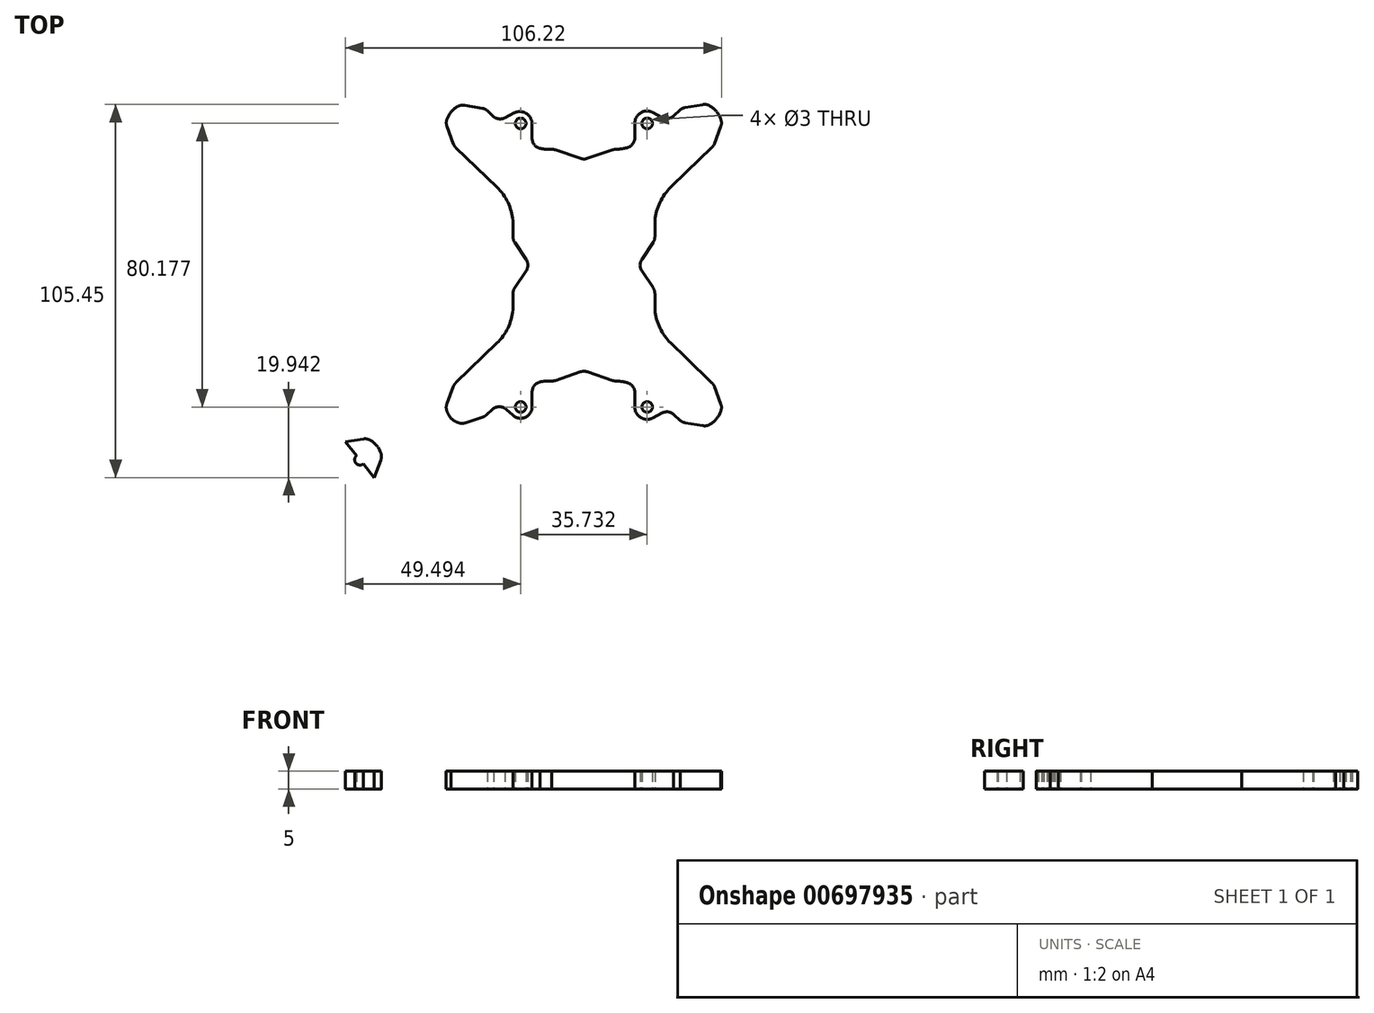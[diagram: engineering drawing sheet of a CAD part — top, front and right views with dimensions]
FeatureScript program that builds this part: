
annotation { "Feature Type Name" : "Feature", "Feature Type Description" : "" }
export const myFeature = defineFeature(function(context is Context, id is Id, definition is map)
    precondition{}
    {
        {
            var Q0;
            Q0=qCreatedBy(makeId("Top.planeOp"),FACE);
            var sketch = newSketch(context, id + "F0", { "sketchPlane" : qUnion([Q0])});
            skArc(sketch, "E0.MirrorCS", {"start": v(27.18, 43.9) * mm, "mid": v(27.85, 44.3) * mm, "end": v(28.6, 44.54) * mm});
            skLineSegment(sketch, "E1.MirrorCS", {"start": v(27.18, 43.9) * mm, "end": v(25.36, 42.14) * mm});
            skArc(sketch, "E2.MirrorCS", {"start": v(38.59, 41.43) * mm, "mid": v(38.86, 40.33) * mm, "end": v(38.7, 39.21) * mm});
            skArc(sketch, "E3.MirrorCS", {"start": v(33.61, 45.38) * mm, "mid": v(34.66, 45.37) * mm, "end": v(35.65, 45) * mm});
            skLineSegment(sketch, "E4.MirrorCS", {"start": v(36.87, 34.33) * mm, "end": v(38.7, 39.21) * mm});
            skLineSegment(sketch, "E5.MirrorCS", {"start": v(28.6, 44.54) * mm, "end": v(33.61, 45.38) * mm});
            skCircle(sketch, "E6.MirrorC", {"center": v(17.87, 40.09) * mm, "radius": 1.5 * mm});
            skArc(sketch, "E7.MirrorCS", {"start": v(35.65, 45) * mm, "mid": v(37.43, 43.47) * mm, "end": v(38.59, 41.43) * mm});
            skArc(sketch, "E8.MirrorCS", {"start": v(14.39, 36.08) * mm, "mid": v(13.74, 34.22) * mm, "end": v(12.09, 33.16) * mm});
            skLineSegment(sketch, "E9.MirrorCS", {"start": v(36.14, 33.23) * mm, "end": v(35.6, 32.7) * mm});
            skArc(sketch, "E10.MirrorCS", {"start": v(36.87, 34.33) * mm, "mid": v(36.57, 33.74) * mm, "end": v(36.14, 33.23) * mm});
            skArc(sketch, "E11.MirrorCS", {"start": v(9, 32.75) * mm, "mid": v(10.56, 32.88) * mm, "end": v(12.09, 33.16) * mm});
            skLineSegment(sketch, "E12.MirrorCS", {"start": v(14.39, 40.46) * mm, "end": v(14.39, 36.08) * mm});
            skLineSegment(sketch, "E13.MirrorCS", {"start": v(19.53, 43.17) * mm, "end": v(22.03, 41.82) * mm});
            skLineSegment(sketch, "E14.MirrorCS", {"start": v(29.02, 26.35) * mm, "end": v(24.57, 22.03) * mm});
            skArc(sketch, "E15.MirrorCS", {"start": v(25.36, 42.14) * mm, "mid": v(23.75, 41.47) * mm, "end": v(22.03, 41.82) * mm});
            skPoint(sketch, "E16.MirrorP", {"position": v(18, 22.67) * mm});
            skPoint(sketch, "E17.MirrorP", {"position": v(18.1, 36.17) * mm});
            skPoint(sketch, "E18.MirrorP", {"position": v(27.93, 44.26) * mm});
            skPoint(sketch, "E19.MirrorP", {"position": v(20, 17.65) * mm});
            skLineSegment(sketch, "E20.MirrorCS", {"start": v(35.6, 32.7) * mm, "end": v(29.02, 26.35) * mm});
            skPoint(sketch, "E21.MirrorP", {"position": v(20, 20) * mm});
            skPoint(sketch, "E22.MirrorP", {"position": v(34.26, 31.4) * mm});
            skPoint(sketch, "E23.MirrorP", {"position": v(18.25, 22.92) * mm});
            skArc(sketch, "E24.MirrorCS", {"start": v(14.39, 40.46) * mm, "mid": v(16.23, 43.18) * mm, "end": v(19.53, 43.17) * mm});
            skPoint(sketch, "E25.MirrorP", {"position": v(34.66, 45.39) * mm});
            skPoint(sketch, "E26.MirrorP", {"position": v(14.39, 33.92) * mm});
            skPoint(sketch, "E27.MirrorP", {"position": v(21.82, 21.5) * mm});
            skPoint(sketch, "E28.MirrorP", {"position": v(39.03, 40.08) * mm});
            skPoint(sketch, "E29.MirrorP", {"position": v(36.63, 33.7) * mm});
            skPoint(sketch, "E30.MirrorP", {"position": v(32.97, 48.4) * mm});
            skPoint(sketch, "E31.MirrorP", {"position": v(23.8, 40.86) * mm});
            skPoint(sketch, "E32.MirrorP", {"position": v(30.36, 27.65) * mm});
            skArc(sketch, "E33.MirrorCS", {"start": v(-27.3, 43.71) * mm, "mid": v(-27.97, 44.13) * mm, "end": v(-28.72, 44.35) * mm});
            skLineSegment(sketch, "E34.MirrorCS", {"start": v(-27.3, 43.71) * mm, "end": v(-25.49, 41.96) * mm});
            skCircle(sketch, "E35.MirrorC", {"center": v(-17.87, 40.09) * mm, "radius": 1.5 * mm});
            skArc(sketch, "E36.MirrorCS", {"start": v(-36.86, 34.3) * mm, "mid": v(-36.56, 33.7) * mm, "end": v(-36.13, 33.2) * mm});
            skLineSegment(sketch, "E37.MirrorCS", {"start": v(-36.13, 33.2) * mm, "end": v(-35.6, 32.67) * mm});
            skArc(sketch, "E38.MirrorCS", {"start": v(-33.74, 45.2) * mm, "mid": v(-34.79, 45.19) * mm, "end": v(-35.77, 44.82) * mm});
            skLineSegment(sketch, "E39.MirrorCS", {"start": v(-36.86, 34.3) * mm, "end": v(-38.7, 39.18) * mm});
            skLineSegment(sketch, "E40.MirrorCS", {"start": v(-28.72, 44.35) * mm, "end": v(-33.74, 45.2) * mm});
            skArc(sketch, "E41.MirrorCS", {"start": v(-38.71, 41.24) * mm, "mid": v(-38.89, 40.2) * mm, "end": v(-38.7, 39.18) * mm});
            skArc(sketch, "E42.MirrorCS", {"start": v(-35.77, 44.82) * mm, "mid": v(-37.55, 43.29) * mm, "end": v(-38.71, 41.24) * mm});
            skLineSegment(sketch, "E43.MirrorCS", {"start": v(-19.8, 42.98) * mm, "end": v(-22.3, 41.63) * mm});
            skArc(sketch, "E44.MirrorCS", {"start": v(-25.49, 41.96) * mm, "mid": v(-23.94, 41.33) * mm, "end": v(-22.3, 41.63) * mm});
            skLineSegment(sketch, "E45.MirrorCS", {"start": v(-29.01, 26.32) * mm, "end": v(-24.57, 22.03) * mm});
            skArc(sketch, "E46.MirrorCS", {"start": v(-14.65, 35.9) * mm, "mid": v(-14, 34.04) * mm, "end": v(-12.35, 32.98) * mm});
            skArc(sketch, "E47.MirrorCS", {"start": v(-14.65, 40.27) * mm, "mid": v(-16.5, 43) * mm, "end": v(-19.8, 42.98) * mm});
            skLineSegment(sketch, "E48.MirrorCS", {"start": v(-14.65, 40.27) * mm, "end": v(-14.65, 35.9) * mm});
            skArc(sketch, "E49.MirrorCS", {"start": v(-20.05, 12.63) * mm, "mid": v(-21.47, 17.74) * mm, "end": v(-24.57, 22.03) * mm});
            skPoint(sketch, "E50.MirrorP", {"position": v(-18.1, 36.17) * mm});
            skLineSegment(sketch, "E51.MirrorCS", {"start": v(-35.6, 32.67) * mm, "end": v(-29.01, 26.32) * mm});
            skArc(sketch, "E52.MirrorCS", {"start": v(-9.14, 32.75) * mm, "mid": v(-10.75, 32.78) * mm, "end": v(-12.35, 32.98) * mm});
            skPoint(sketch, "E53.MirrorP", {"position": v(-20, 20) * mm});
            skPoint(sketch, "E54.MirrorP", {"position": v(-27.93, 44.26) * mm});
            skPoint(sketch, "E55.MirrorP", {"position": v(-20, 17.65) * mm});
            skPoint(sketch, "E56.MirrorP", {"position": v(-32.97, 48.4) * mm});
            skPoint(sketch, "E57.MirrorP", {"position": v(-30.36, 27.65) * mm});
            skPoint(sketch, "E58.MirrorP", {"position": v(-21.82, 21.5) * mm});
            skPoint(sketch, "E59.MirrorP", {"position": v(-23.8, 40.86) * mm});
            skPoint(sketch, "E60.MirrorP", {"position": v(-39.03, 40.08) * mm});
            skPoint(sketch, "E61.MirrorP", {"position": v(-34.26, 31.4) * mm});
            skPoint(sketch, "E62.MirrorP", {"position": v(-18, 22.67) * mm});
            skPoint(sketch, "E63.MirrorP", {"position": v(-14.39, 33.92) * mm});
            skPoint(sketch, "E64.MirrorP", {"position": v(-18.25, 22.92) * mm});
            skPoint(sketch, "E65.MirrorP", {"position": v(-36.63, 33.7) * mm});
            skPoint(sketch, "E66.MirrorP", {"position": v(-34.66, 45.39) * mm});
            skLineSegment(sketch, "E67.MirrorCS", {"start": v(-8.13, 32.6) * mm, "end": v(-0.97, 30.16) * mm});
            skLineSegment(sketch, "E68.MirrorCS", {"start": v(0.97, 30.16) * mm, "end": v(8.13, 32.6) * mm});
            skArc(sketch, "E69.MirrorCS", {"start": v(-9.14, 32.75) * mm, "mid": v(-8.63, 32.72) * mm, "end": v(-8.13, 32.6) * mm});
            skArc(sketch, "E70.MirrorCS", {"start": v(8.13, 32.6) * mm, "mid": v(8.56, 32.7) * mm, "end": v(9, 32.75) * mm});
            skArc(sketch, "E71.MirrorCS", {"start": v(0.97, 30.16) * mm, "mid": v(0, 30) * mm, "end": v(-0.97, 30.16) * mm});
            skPoint(sketch, "E72.orphan", {"position": v(8.57, 32.75) * mm});
            skPoint(sketch, "E73.orphan", {"position": v(-9.7, 32.74) * mm});
            skLineSegment(sketch, "E74", {"start": v(0, 30.16) * mm, "end": v(0, 30) * mm});
            skPoint(sketch, "E74.startSnap0", {"position": v(0, 30) * mm});
            skArc(sketch, "E75.MirrorCS", {"start": v(20.05, 12.63) * mm, "mid": v(21.47, 17.74) * mm, "end": v(24.57, 22.03) * mm});
            skLineSegment(sketch, "E76", {"start": v(-19.55, 6.41) * mm, "end": v(-16.36, 1.67) * mm});
            skLineSegment(sketch, "E77.MirrorCS", {"start": v(19.55, 6.41) * mm, "end": v(16.36, 1.67) * mm});
            skLineSegment(sketch, "E78.trimOffspring", {"start": v(-20.05, 8.08) * mm, "end": v(-20.05, 12.63) * mm});
            skLineSegment(sketch, "E79.trimOffspring", {"start": v(20.05, 8.08) * mm, "end": v(20.05, 12.63) * mm});
            skPoint(sketch, "E80.visualSharp", {"position": v(-20.05, 7.17) * mm});
            skArc(sketch, "E80.filletArc", {"start": v(-20.05, 8.08) * mm, "mid": v(-19.92, 7.21) * mm, "end": v(-19.55, 6.41) * mm});
            skPoint(sketch, "E81.visualSharp", {"position": v(-15.24, 0) * mm});
            skArc(sketch, "E81.filletArc", {"start": v(-16.36, -1.67) * mm, "mid": v(-15.85, 0) * mm, "end": v(-16.36, 1.67) * mm});
            skPoint(sketch, "E82.visualSharp", {"position": v(20.05, 7.17) * mm});
            skArc(sketch, "E82.filletArc", {"start": v(19.55, 6.41) * mm, "mid": v(19.92, 7.21) * mm, "end": v(20.05, 8.08) * mm});
            skPoint(sketch, "E83.visualSharp", {"position": v(15.24, 0) * mm});
            skArc(sketch, "E83.filletArc", {"start": v(16.36, 1.67) * mm, "mid": v(15.85, 0) * mm, "end": v(16.36, -1.67) * mm});
            skLineSegment(sketch, "E84.bottom", {"start": v(-19.98, 42.28) * mm, "end": v(19.98, 42.28) * mm, "construction": true});
            skLineSegment(sketch, "E84.left", {"start": v(-19.98, 42.28) * mm, "end": v(-19.98, -42.28) * mm, "construction": true});
            skLineSegment(sketch, "E84.right", {"start": v(19.98, 42.28) * mm, "end": v(19.98, -42.28) * mm, "construction": true});
            skPoint(sketch, "E84.middle", {"position": v(0, 0) * mm});
            skLineSegment(sketch, "E85.MirrorCS", {"start": v(0, -30.16) * mm, "end": v(0, -30) * mm});
            skLineSegment(sketch, "E86.MirrorCS", {"start": v(0.97, -30.16) * mm, "end": v(8.13, -32.6) * mm});
            skArc(sketch, "E87.MirrorCS", {"start": v(-36.86, -34.3) * mm, "mid": v(-36.56, -33.7) * mm, "end": v(-36.13, -33.2) * mm});
            skLineSegment(sketch, "E88.MirrorCS", {"start": v(36.14, -33.23) * mm, "end": v(35.6, -32.7) * mm});
            skArc(sketch, "E89.MirrorCS", {"start": v(-9.14, -32.75) * mm, "mid": v(-8.63, -32.72) * mm, "end": v(-8.13, -32.6) * mm});
            skArc(sketch, "E90.MirrorCS", {"start": v(8.13, -32.6) * mm, "mid": v(8.56, -32.7) * mm, "end": v(9, -32.75) * mm});
            skArc(sketch, "E91.MirrorCS", {"start": v(-9.14, -32.75) * mm, "mid": v(-10.75, -32.78) * mm, "end": v(-12.35, -32.98) * mm});
            skArc(sketch, "E92.MirrorCS", {"start": v(0.97, -30.16) * mm, "mid": v(0, -30) * mm, "end": v(-0.97, -30.16) * mm});
            skLineSegment(sketch, "E93.MirrorCS", {"start": v(-36.13, -33.2) * mm, "end": v(-35.6, -32.67) * mm});
            skArc(sketch, "E94.MirrorCS", {"start": v(36.87, -34.33) * mm, "mid": v(36.57, -33.74) * mm, "end": v(36.14, -33.23) * mm});
            skArc(sketch, "E95.MirrorCS", {"start": v(9, -32.75) * mm, "mid": v(10.56, -32.88) * mm, "end": v(12.09, -33.16) * mm});
            skArc(sketch, "E96.MirrorCS", {"start": v(-20.05, -8.08) * mm, "mid": v(-19.92, -7.21) * mm, "end": v(-19.55, -6.41) * mm});
            skLineSegment(sketch, "E97.MirrorCS", {"start": v(36.87, -34.33) * mm, "end": v(38.7, -39.21) * mm});
            skLineSegment(sketch, "E98.MirrorCS", {"start": v(27.18, -43.9) * mm, "end": v(25.36, -42.14) * mm});
            skArc(sketch, "E99.MirrorCS", {"start": v(25.36, -42.14) * mm, "mid": v(23.75, -41.47) * mm, "end": v(22.03, -41.82) * mm});
            skLineSegment(sketch, "E100.MirrorCS", {"start": v(19.53, -43.17) * mm, "end": v(22.03, -41.82) * mm});
            skArc(sketch, "E101.MirrorCS", {"start": v(38.59, -41.43) * mm, "mid": v(38.86, -40.33) * mm, "end": v(38.7, -39.21) * mm});
            skArc(sketch, "E102.MirrorCS", {"start": v(27.18, -43.9) * mm, "mid": v(27.85, -44.3) * mm, "end": v(28.6, -44.54) * mm});
            skLineSegment(sketch, "E103.MirrorCS", {"start": v(-20.05, -8.08) * mm, "end": v(-20.05, -12.63) * mm});
            skLineSegment(sketch, "E104.MirrorCS", {"start": v(20.05, -8.08) * mm, "end": v(20.05, -12.63) * mm});
            skLineSegment(sketch, "E105.MirrorCS", {"start": v(-35.6, -32.67) * mm, "end": v(-29.01, -26.32) * mm});
            skArc(sketch, "E106.MirrorCS", {"start": v(19.55, -6.41) * mm, "mid": v(19.92, -7.21) * mm, "end": v(20.05, -8.08) * mm});
            skCircle(sketch, "E107.MirrorC", {"center": v(17.87, -40.09) * mm, "radius": 1.5 * mm});
            skLineSegment(sketch, "E108.MirrorCS", {"start": v(19.55, -6.41) * mm, "end": v(16.36, -1.67) * mm});
            skArc(sketch, "E109.MirrorCS", {"start": v(-14.65, -35.9) * mm, "mid": v(-14, -34.04) * mm, "end": v(-12.35, -32.98) * mm});
            skArc(sketch, "E110.MirrorCS", {"start": v(20.05, -12.63) * mm, "mid": v(21.47, -17.74) * mm, "end": v(24.57, -22.03) * mm});
            skArc(sketch, "E111.MirrorCS", {"start": v(35.65, -45) * mm, "mid": v(37.43, -43.47) * mm, "end": v(38.59, -41.43) * mm});
            skArc(sketch, "E112.MirrorCS", {"start": v(-37.55, -43.29) * mm, "mid": v(-38.22, -42.32) * mm, "end": v(-38.71, -41.24) * mm});
            skLineSegment(sketch, "E113.MirrorCS", {"start": v(14.39, -40.46) * mm, "end": v(14.39, -36.08) * mm});
            skLineSegment(sketch, "E114.MirrorCS", {"start": v(29.02, -26.35) * mm, "end": v(24.57, -22.03) * mm});
            skLineSegment(sketch, "E115.MirrorCS", {"start": v(-8.13, -32.6) * mm, "end": v(-0.97, -30.16) * mm});
            skArc(sketch, "E116.MirrorCS", {"start": v(14.39, -40.46) * mm, "mid": v(16.23, -43.18) * mm, "end": v(19.53, -43.17) * mm});
            skArc(sketch, "E117.MirrorCS", {"start": v(-38.71, -41.24) * mm, "mid": v(-38.89, -40.2) * mm, "end": v(-38.7, -39.18) * mm});
            skLineSegment(sketch, "E118.MirrorCS", {"start": v(35.6, -32.7) * mm, "end": v(29.02, -26.35) * mm});
            skArc(sketch, "E119.MirrorCS", {"start": v(-20.05, -12.63) * mm, "mid": v(-21.47, -17.74) * mm, "end": v(-24.57, -22.03) * mm});
            skLineSegment(sketch, "E120.MirrorCS", {"start": v(-29.01, -26.32) * mm, "end": v(-24.57, -22.03) * mm});
            skCircle(sketch, "E121.MirrorC", {"center": v(-17.87, -40.09) * mm, "radius": 1.5 * mm});
            skArc(sketch, "E122.MirrorCS", {"start": v(14.39, -36.08) * mm, "mid": v(13.74, -34.22) * mm, "end": v(12.09, -33.16) * mm});
            skArc(sketch, "E123.MirrorCS", {"start": v(33.61, -45.38) * mm, "mid": v(34.66, -45.37) * mm, "end": v(35.65, -45) * mm});
            skLineSegment(sketch, "E124.MirrorCS", {"start": v(-14.65, -40.27) * mm, "end": v(-14.65, -35.9) * mm});
            skLineSegment(sketch, "E125.MirrorCS", {"start": v(28.6, -44.54) * mm, "end": v(33.61, -45.38) * mm});
            skArc(sketch, "E126.MirrorCS", {"start": v(-14.65, -40.27) * mm, "mid": v(-14.69, -40.56) * mm, "end": v(-14.76, -40.84) * mm});
            skLineSegment(sketch, "E127.MirrorCS", {"start": v(-36.86, -34.3) * mm, "end": v(-38.7, -39.18) * mm});
            skLineSegment(sketch, "E128.MirrorCS", {"start": v(-19.55, -6.41) * mm, "end": v(-16.36, -1.67) * mm});
            skPoint(sketch, "E129.MirrorP", {"position": v(23.8, -40.86) * mm});
            skPoint(sketch, "E130.MirrorP", {"position": v(20, -20) * mm});
            skPoint(sketch, "E131.MirrorP", {"position": v(-18.1, -36.17) * mm});
            skPoint(sketch, "E132.MirrorP", {"position": v(18.1, -36.17) * mm});
            skPoint(sketch, "E133.MirrorP", {"position": v(8.57, -32.75) * mm});
            skPoint(sketch, "E134.MirrorP", {"position": v(-27.93, -44.26) * mm});
            skPoint(sketch, "E135.MirrorP", {"position": v(-20, -17.65) * mm});
            skPoint(sketch, "E136.MirrorP", {"position": v(20, -17.65) * mm});
            skPoint(sketch, "E137.MirrorP", {"position": v(27.93, -44.26) * mm});
            skPoint(sketch, "E138.MirrorP", {"position": v(-20.05, -7.17) * mm});
            skPoint(sketch, "E139.MirrorP", {"position": v(18.25, -22.92) * mm});
            skPoint(sketch, "E140.MirrorP", {"position": v(39.03, -40.08) * mm});
            skPoint(sketch, "E141.MirrorP", {"position": v(-34.66, -45.39) * mm});
            skPoint(sketch, "E142.MirrorP", {"position": v(-9.7, -32.74) * mm});
            skPoint(sketch, "E143.MirrorP", {"position": v(14.39, -33.92) * mm});
            skPoint(sketch, "E144.MirrorP", {"position": v(-18.25, -22.92) * mm});
            skPoint(sketch, "E145.MirrorP", {"position": v(0, -30) * mm});
            skPoint(sketch, "E146.MirrorP", {"position": v(-30.36, -27.65) * mm});
            skLineSegment(sketch, "E147.MirrorCS", {"start": v(-19.98, -42.28) * mm, "end": v(19.98, -42.28) * mm, "construction": true});
            skPoint(sketch, "E148.MirrorP", {"position": v(-18, -22.67) * mm});
            skPoint(sketch, "E149.MirrorP", {"position": v(-21.82, -21.5) * mm});
            skPoint(sketch, "E150.MirrorP", {"position": v(21.82, -21.5) * mm});
            skPoint(sketch, "E151.MirrorP", {"position": v(-34.26, -31.4) * mm});
            skPoint(sketch, "E152.MirrorP", {"position": v(36.63, -33.7) * mm});
            skPoint(sketch, "E153.MirrorP", {"position": v(34.66, -45.39) * mm});
            skPoint(sketch, "E154.MirrorP", {"position": v(-36.63, -33.7) * mm});
            skPoint(sketch, "E155.MirrorP", {"position": v(-32.97, -48.4) * mm});
            skPoint(sketch, "E156.MirrorP", {"position": v(18, -22.67) * mm});
            skPoint(sketch, "E157.MirrorP", {"position": v(32.97, -48.4) * mm});
            skPoint(sketch, "E158.MirrorP", {"position": v(30.36, -27.65) * mm});
            skPoint(sketch, "E159.MirrorP", {"position": v(20.05, -7.17) * mm});
            skPoint(sketch, "E160.MirrorP", {"position": v(-14.39, -33.92) * mm});
            skPoint(sketch, "E161.MirrorP", {"position": v(-39.03, -40.08) * mm});
            skPoint(sketch, "E162.MirrorP", {"position": v(34.26, -31.4) * mm});
            skPoint(sketch, "E163.MirrorP", {"position": v(-20, -20) * mm});
            skArc(sketch, "E164.MirrorCS", {"start": v(-59.22, -60.03) * mm, "mid": v(-59.52, -60.62) * mm, "end": v(-59.95, -61.13) * mm});
            skLineSegment(sketch, "E165.MirrorCS", {"start": v(-59.95, -61.13) * mm, "end": v(-60.49, -61.66) * mm});
            skLineSegment(sketch, "E166.MirrorCS", {"start": v(-60.49, -61.66) * mm, "end": v(-67.07, -68) * mm});
            skArc(sketch, "E167.MirrorCS", {"start": v(-62.34, -49.13) * mm, "mid": v(-61.3, -49.14) * mm, "end": v(-60.3, -49.5) * mm});
            skLineSegment(sketch, "E168.MirrorCS", {"start": v(-67.36, -49.97) * mm, "end": v(-62.34, -49.13) * mm});
            skArc(sketch, "E169.MirrorCS", {"start": v(-60.3, -49.5) * mm, "mid": v(-58.53, -51.04) * mm, "end": v(-57.37, -53.08) * mm});
            skArc(sketch, "E170.MirrorCS", {"start": v(-57.37, -53.08) * mm, "mid": v(-57.2, -54.12) * mm, "end": v(-57.38, -55.15) * mm});
            skArc(sketch, "E171.MirrorCS", {"start": v(-68.77, -50.61) * mm, "mid": v(-68.1, -50.2) * mm, "end": v(-67.36, -49.97) * mm});
            skLineSegment(sketch, "E172.MirrorCS", {"start": v(-59.22, -60.03) * mm, "end": v(-57.38, -55.15) * mm});
            skPoint(sketch, "E173.MirrorP", {"position": v(-68.14, -50.07) * mm});
            skPoint(sketch, "E174.MirrorP", {"position": v(-61.42, -48.94) * mm});
            skPoint(sketch, "E175.MirrorP", {"position": v(-59.45, -60.63) * mm});
            skPoint(sketch, "E176.MirrorP", {"position": v(-63.11, -45.93) * mm});
            skPoint(sketch, "E177.MirrorP", {"position": v(-57.05, -54.25) * mm});
            skLineSegment(sketch, "E178", {"start": v(-59.22, -60.03) * mm, "end": v(-67.36, -49.97) * mm});
            skPoint(sketch, "E179", {"position": v(-63.3, -55) * mm});
            skCircle(sketch, "E180", {"center": v(-63.3, -55) * mm, "radius": 1.5 * mm});
            skLineSegment(sketch, "E181", {"start": v(-63.3, -55) * mm, "end": v(-69.86, -61.34) * mm});
            skLineSegment(sketch, "E182.MirrorCS", {"start": v(-69.84, -51.96) * mm, "end": v(-76.42, -58.31) * mm});
            skLineSegment(sketch, "E183", {"start": v(-37.55, -43.29) * mm, "end": v(19.17, 11.45) * mm, "construction": true});
            skLineSegment(sketch, "E184.MirrorCS", {"start": v(-28.54, -42.91) * mm, "end": v(-33.49, -44.58) * mm});
            skArc(sketch, "E185.MirrorCS", {"start": v(-35.55, -44.52) * mm, "mid": v(-34.52, -44.73) * mm, "end": v(-33.49, -44.58) * mm});
            skArc(sketch, "E186.MirrorCS", {"start": v(-37.55, -43.29) * mm, "mid": v(-36.6, -44) * mm, "end": v(-35.55, -44.52) * mm});
            skPoint(sketch, "E187.orphan", {"position": v(-39.02, -41.45) * mm});
            skPoint(sketch, "E188.MirrorCS.end.orphan", {"position": v(-35.77, -44.82) * mm});
            skPoint(sketch, "E189.MirrorCS.end.orphan", {"position": v(-33.74, -45.2) * mm});
            skPoint(sketch, "E190.MirrorCS.end.orphan", {"position": v(-28.72, -44.35) * mm});
            skPoint(sketch, "E191.MirrorCS.start.orphan", {"position": v(-27.3, -43.71) * mm});
            skArc(sketch, "E192.MirrorCS", {"start": v(-28.54, -42.91) * mm, "mid": v(-27.94, -42.63) * mm, "end": v(-27.41, -42.23) * mm});
            skLineSegment(sketch, "E193.MirrorCS", {"start": v(-27.41, -42.23) * mm, "end": v(-26.87, -41.7) * mm});
            skPoint(sketch, "E194.MirrorCS.start.orphan", {"position": v(-25.49, -41.96) * mm});
            skLineSegment(sketch, "E195", {"start": v(-26.87, -41.7) * mm, "end": v(-26.02, -40.88) * mm});
            skPoint(sketch, "E196.visualSharp", {"position": v(-19.8, -42.98) * mm});
            skArc(sketch, "E197.0", {"start": v(-14.76, -40.84) * mm, "mid": v(-16.95, -43.15) * mm, "end": v(-20.05, -42.42) * mm});
            skLineSegment(sketch, "E198", {"start": v(-21.97, -40.77) * mm, "end": v(-20.05, -42.42) * mm});
            skPoint(sketch, "E199.visualSharp", {"position": v(-24.05, -38.98) * mm});
            skArc(sketch, "E199.filletArc", {"start": v(-21.97, -40.77) * mm, "mid": v(-24.02, -40.04) * mm, "end": v(-26.02, -40.88) * mm});
            skSolve(sketch);
        }
        {
            var Q0;
            Q0 = qSketchRegion(id + "F0", true);
            extrude(context, id + "F1", {"entities" : qUnion([Q0]), "depth" : 5 * mm, "offsetDistance" : 25 * mm});
        }
    });
